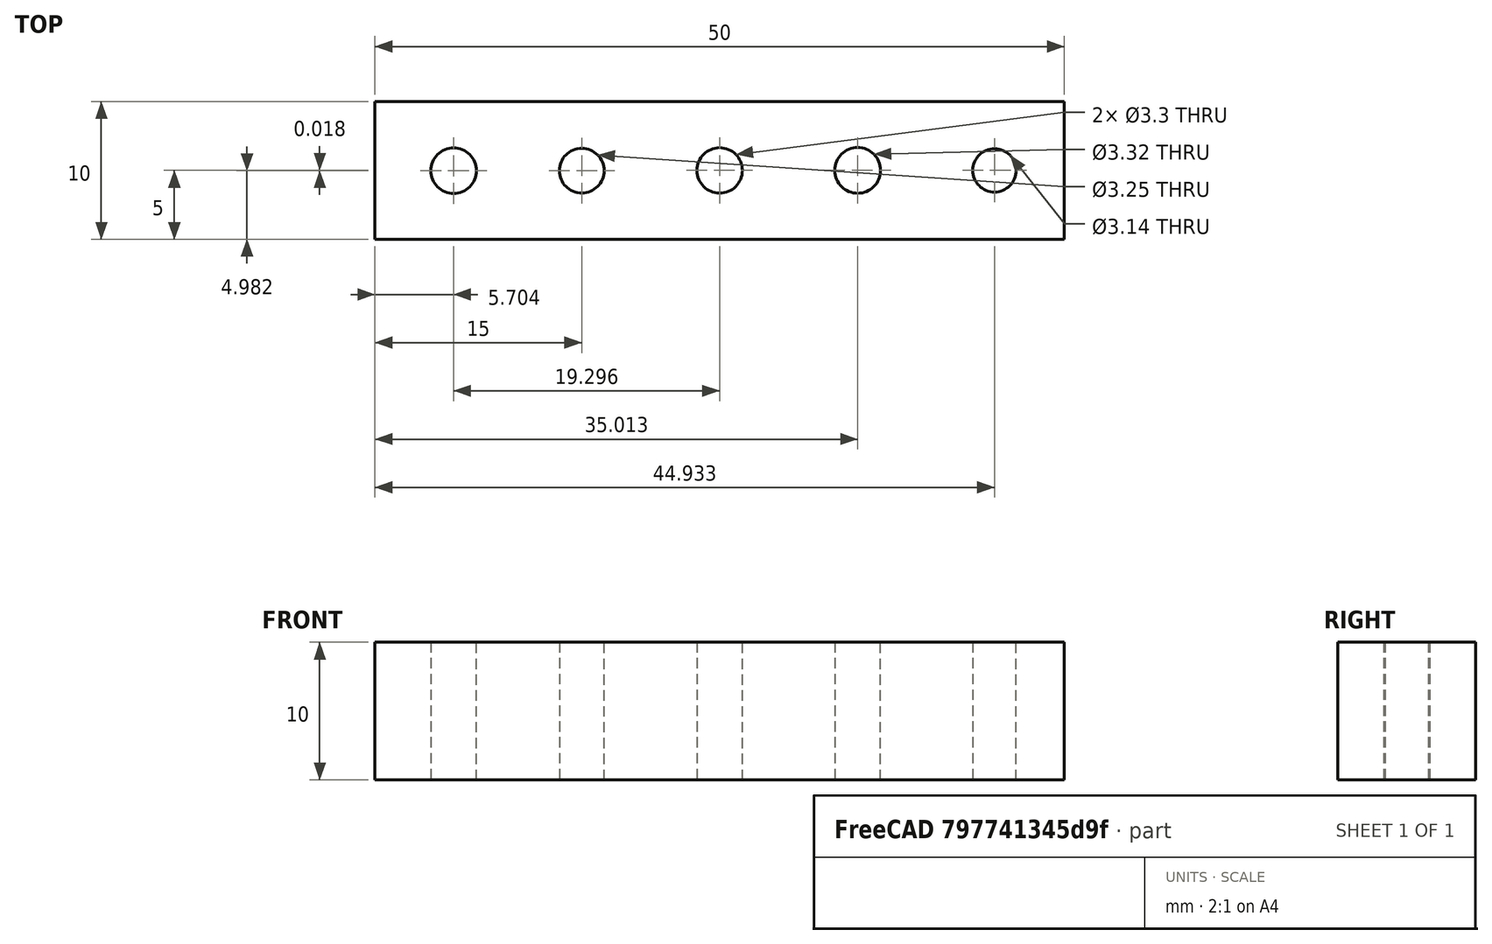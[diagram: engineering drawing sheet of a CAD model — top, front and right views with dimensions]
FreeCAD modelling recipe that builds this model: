
FCSTD DOCUMENT  (FreeCAD 0.20R29410 (Git))
Label: ladron_croqueado
License: All rights reserved
LicenseURL: http://en.wikipedia.org/wiki/All_rights_reserved
objects: Sketcher::SketchObject×1, Part::Extrusion×1
note: 2 computed .brp shape members not serialized (recipe doc carries the construction recipe); baked Part::Feature solids carry a one-line shape summary decoded from their .brp

FEATURE [Sketcher::SketchObject] Sketch
  FullyConstrained = false
  sketch-geometry (9):
    g0: LineSegment StartX=-25 StartY=5 StartZ=0 EndX=25 EndY=5 EndZ=0
    g1: LineSegment StartX=25 StartY=5 StartZ=0 EndX=25 EndY=-5 EndZ=0
    g2: LineSegment StartX=25 StartY=-5 StartZ=0 EndX=-25 EndY=-5 EndZ=0
    g3: LineSegment StartX=-25 StartY=-5 StartZ=0 EndX=-25 EndY=5 EndZ=0
    g4: Circle CenterX=0 CenterY=0 CenterZ=0 NormalX=0 NormalY=0 NormalZ=1 AngleXU=0 Radius=1.65
    g5: Circle CenterX=-10 CenterY=-0.018389 CenterZ=0 NormalX=0 NormalY=0 NormalZ=1 AngleXU=0 Radius=1.62315
    g6: Circle CenterX=-19.296 CenterY=-0.018389 CenterZ=0 NormalX=0 NormalY=0 NormalZ=1 AngleXU=0 Radius=1.65
    g7: Circle CenterX=10.0129 CenterY=0 CenterZ=0 NormalX=0 NormalY=0 NormalZ=1 AngleXU=0 Radius=1.66046
    g8: Circle CenterX=19.933 CenterY=0 CenterZ=0 NormalX=0 NormalY=0 NormalZ=1 AngleXU=0 Radius=1.56887
  constraints (17):
    c: Coincident(g0,g1)
    c: Coincident(g1,g2)
    c: Coincident(g2,g3)
    c: Coincident(g3,g0)
    c: Horizontal(g0)
    c: Horizontal(g2)
    c: Vertical(g1)
    c: Vertical(g3)
    c: DistanceX(g2,g2) = 50
    c: DistanceY(g3,g3) = 10
    c: Symmetric(g0,g1,g-1)
    c: Coincident(g4,g-1)
    c: Diameter(g4) = 3.3
    c: DistanceX(g5,g4) = 10
    c: Diameter(g6) = 3.3
    c: PointOnObject(g7,g-1)
    c: PointOnObject(g8,g-1)
FEATURE [Part::Extrusion] Extrude
  Base = -> Sketch
  Dir = (0,0,1)
  DirMode = 2
  FaceMakerClass = Part::FaceMakerBullseye
  LengthFwd = 10
  LengthRev = 0
  Solid = true
  Symmetric = false
